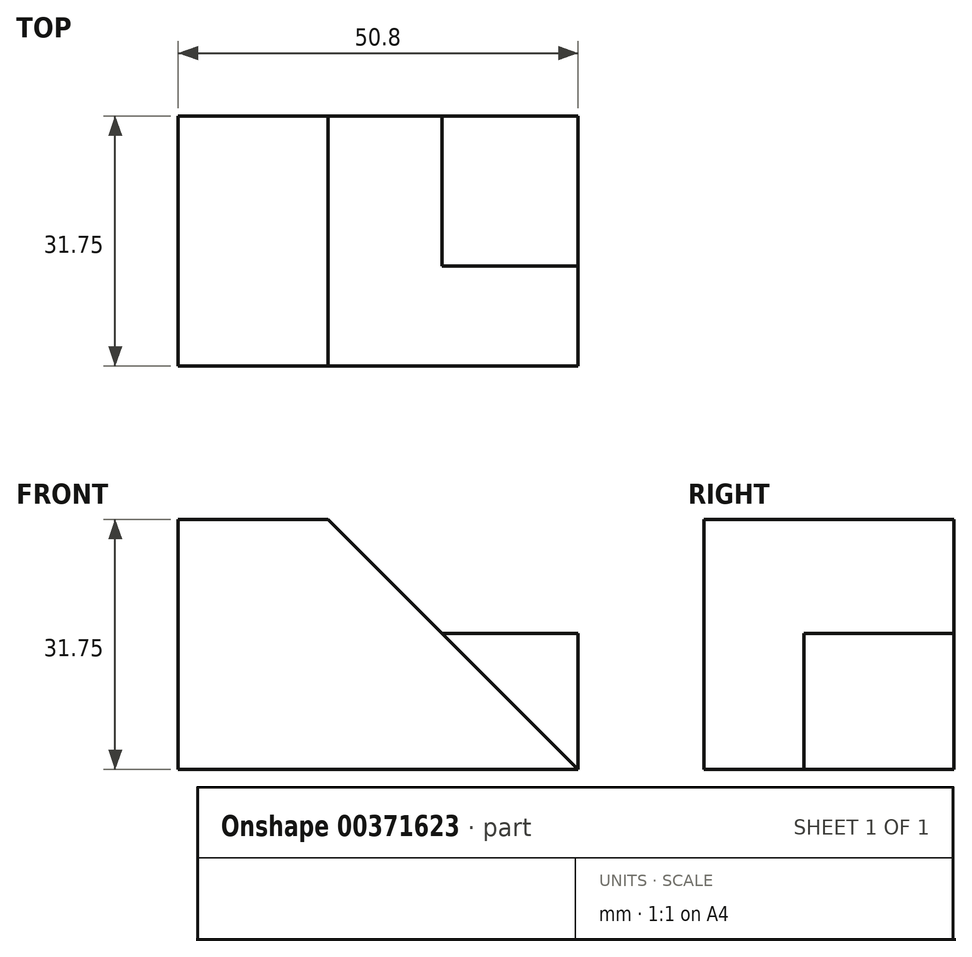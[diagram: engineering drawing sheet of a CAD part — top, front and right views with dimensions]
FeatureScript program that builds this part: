
annotation { "Feature Type Name" : "Feature", "Feature Type Description" : "" }
export const myFeature = defineFeature(function(context is Context, id is Id, definition is map)
    precondition{}
    {
        {
            var Q0;
            Q0=qCreatedBy(makeId("Front.planeOp"),FACE);
            var sketch = newSketch(context, id + "F0", { "sketchPlane" : qUnion([Q0])});
            skLineSegment(sketch, "E0", {"start": v(0, 0) * mm, "end": v(50.8, 0) * mm});
            skLineSegment(sketch, "E1", {"start": v(50.8, 0) * mm, "end": v(50.8, 31.75) * mm});
            skLineSegment(sketch, "E2", {"start": v(50.8, 31.75) * mm, "end": v(0, 31.75) * mm});
            skLineSegment(sketch, "E3", {"start": v(0, 31.75) * mm, "end": v(0, 0) * mm});
            skSolve(sketch);
        }
        {
            var Q0;
            Q0=makeQuery(id+"F0.imprint","IMPRINT",FACE,{"disambiguationData":[TD([[makeQuery(id+"F0.imprint","IMPRINT",EDGE,{"derivedFrom":sQuery(id+"F0.wireOp",EDGE,"E0")}),1.0]])]});
            extrude(context, id + "F1", {"entities" : qUnion([Q0]), "depth" : 31.75 * mm});
        }
        {
            var Q0;
            Q0=makeQuery(id+"F1.opExtrude","CAP_FACE",FACE,{"disambiguationData":[OSD([sQuery(id+"F0.wireOp",EDGE,"E0"),sQuery(id+"F0.wireOp",EDGE,"E1"),sQuery(id+"F0.wireOp",EDGE,"E2"),sQuery(id+"F0.wireOp",EDGE,"E3")])],"isStart":false});
            var sketch = newSketch(context, id + "F2", { "sketchPlane" : qUnion([Q0])});
            skLineSegment(sketch, "E4", {"start": v(19.05, 31.75) * mm, "end": v(50.8, 0) * mm});
            skSolve(sketch);
        }
        {
            var Q0;
            {var subQ0=sQuery(id+"F2.wireOp",EDGE,"E4");Q0=makeQuery(id+"F2.imprint","IMPRINT",FACE,{"disambiguationData":[TD([[makeQuery(id+"F2.imprint","IMPRINT",EDGE,{"derivedFrom":subQ0}),1.0]])]});}
            extrude(context, id + "F3", {"entities" : qUnion([Q0]), "operationType" : NewBodyOperationType.REMOVE, "oppositeDirection" : true, "depth" : 12.7 * mm});
        }
        {
            var Q0;
            Q0=makeQuery(id+"F1.opExtrude","CAP_FACE",FACE,{"disambiguationData":[OSD([sQuery(id+"F0.wireOp",EDGE,"E0"),sQuery(id+"F0.wireOp",EDGE,"E1"),sQuery(id+"F0.wireOp",EDGE,"E2"),sQuery(id+"F0.wireOp",EDGE,"E3")])],"isStart":true});
            var sketch = newSketch(context, id + "F4", { "sketchPlane" : qUnion([Q0])});
            skLineSegment(sketch, "E5", {"start": v(-25.4, 31.75) * mm, "end": v(-38.1, 17.27) * mm});
            skLineSegment(sketch, "E6", {"start": v(-38.1, 17.27) * mm, "end": v(-50.8, 17.27) * mm});
            skSolve(sketch);
        }
        {
            var Q0;
            {var subQ0=sQuery(id+"F4.wireOp",EDGE,"E5");Q0=makeQuery(id+"F4.imprint","IMPRINT",FACE,{"disambiguationData":[TD([[makeQuery(id+"F4.imprint","IMPRINT",EDGE,{"derivedFrom":subQ0}),-1.0]])]});}
            extrude(context, id + "F5", {"entities" : qUnion([Q0]), "operationType" : NewBodyOperationType.REMOVE, "oppositeDirection" : true, "depth" : 25.4 * mm});
        }
        {
            var Q0;
            Q0=makeQuery(id+"F3.boolean.opBoolean","COPY",FACE,{"derivedFrom":makeQuery(id+"F3.opExtrude","CAP_FACE",FACE,{"disambiguationData":[OSD([sQuery(id+"F0.wireOp",EDGE,"E1"),sQuery(id+"F0.wireOp",EDGE,"E2"),sQuery(id+"F2.wireOp",EDGE,"E4")])],"isStart":false})});
            var sketch = newSketch(context, id + "F6", { "sketchPlane" : qUnion([Q0])});
            skLineSegment(sketch, "E7", {"start": v(38.1, 17.27) * mm, "end": v(33.53, 17.27) * mm});
            skLineSegment(sketch, "E8", {"start": v(33.53, 17.27) * mm, "end": v(19.05, 31.75) * mm});
            skSolve(sketch);
        }
        {
            var Q0;
            Q0=makeQuery(id+"F6.imprint","IMPRINT",FACE,{"disambiguationData":[TD([[makeQuery(id+"F6.imprint","IMPRINT",EDGE,{"derivedFrom":sQuery(id+"F6.wireOp",EDGE,"E7")}),-1.0]])]});
            extrude(context, id + "F7", {"entities" : qUnion([Q0]), "operationType" : NewBodyOperationType.REMOVE, "oppositeDirection" : true, "depth" : 25.4 * mm});
        }
    });
